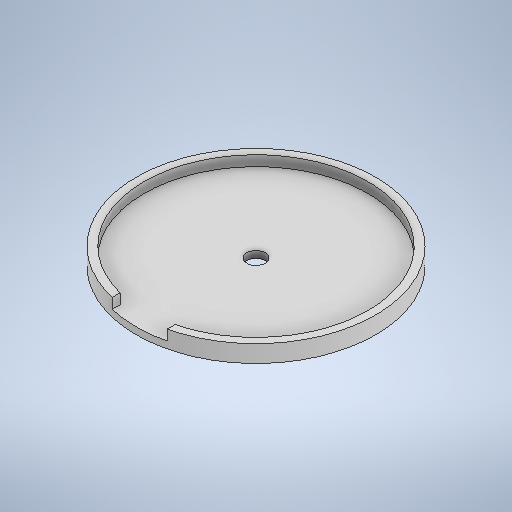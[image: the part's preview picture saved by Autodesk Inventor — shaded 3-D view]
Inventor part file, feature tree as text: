
AUTODESK INVENTOR PART (.ipt)
format: ipt  version: 2025.1 (Build 291241000, 241)  size: 262,656 bytes
history: native  units: mm
features: extrude x4, sketch x4
ambient origin geometry x8: Origin, YZ Plane, XZ Plane, XY Plane, X Axis, Y Axis, Z Axis, Center Point
bodies: Volumenkörper1 (feature_tree)
feature tree (8):
  extrude  "Extrusion1"  Depth=5.0mm TaperAngle=0.0deg
  extrude  "Extrusion2"  Depth=3.0mm TaperAngle=0.0deg
  extrude  "Extrusion3"  TaperAngle=0.0deg  [1 undecoded]
  extrude  "Extrusion4"  Depth=16.0mm
  sketch  "Skizze1"  dims[d0=69.55mm d1=5.0mm d2=0.0mm]
  sketch  "Skizze2"  dims[d3=65.08mm d4=3.0mm d5=0.0mm]
  sketch  "Skizze3"  dims[d6=5.38mm d7=0.0mm d8=0.0mm]
  sketch  "Skizze4"  dims[d9=16.0mm d10=16.0mm d11=10.0mm d12=0.0mm]
note: 1 required parameter value undecoded (feature->parameter linkage not recoverable at this tier; creation-order binding heuristic only, values carry confidence <= 0.55)
